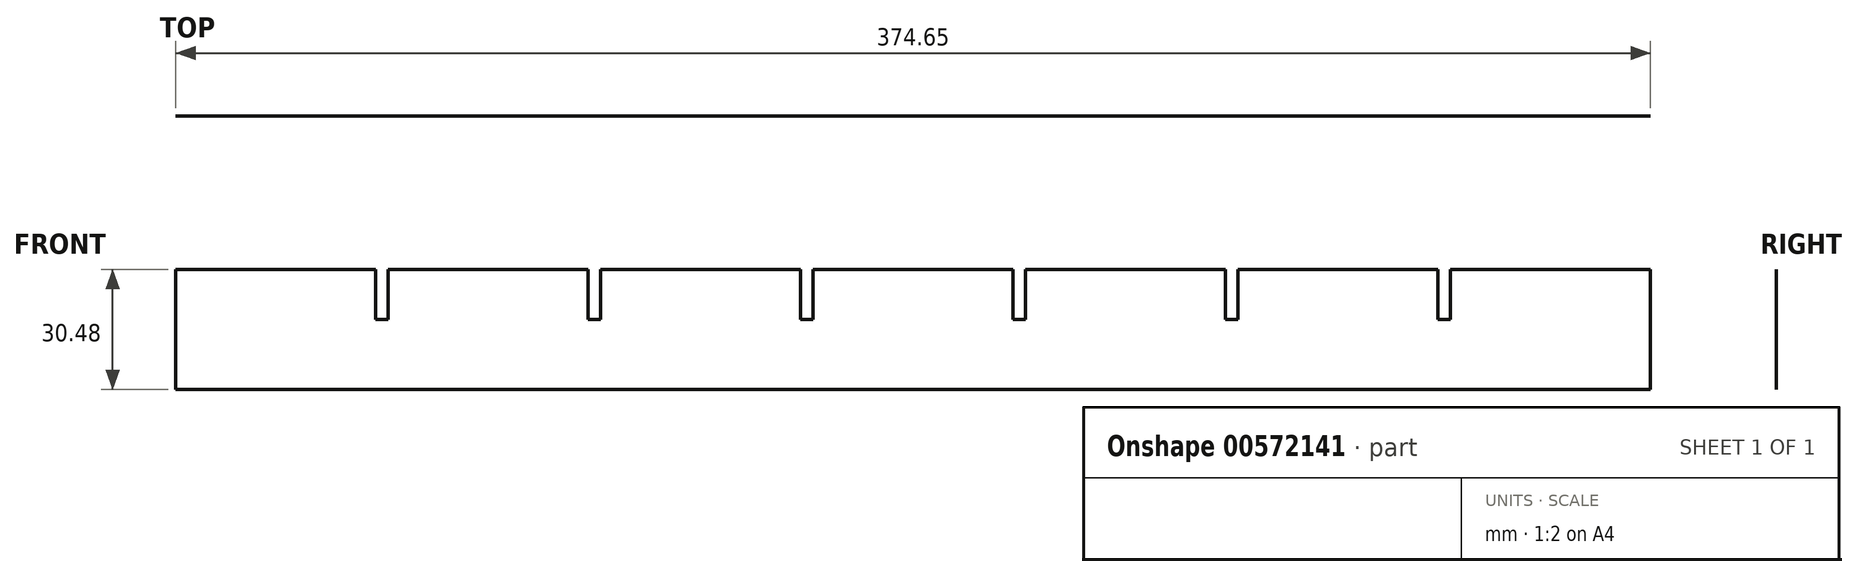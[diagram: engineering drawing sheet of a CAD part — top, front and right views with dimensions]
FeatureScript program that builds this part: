
annotation { "Feature Type Name" : "Feature", "Feature Type Description" : "" }
export const myFeature = defineFeature(function(context is Context, id is Id, definition is map)
    precondition{}
    {
        {
            var Q0;
            Q0=qCreatedBy(makeId("Front.planeOp"),FACE);
            var sketch = newSketch(context, id + "F0", { "sketchPlane" : qUnion([Q0])});
            skLineSegment(sketch, "E0.bottom", {"start": v(-281.33, -49.02) * mm, "end": v(93.32, -49.02) * mm});
            skLineSegment(sketch, "E0.top", {"start": v(-281.33, -79.5) * mm, "end": v(93.32, -79.5) * mm});
            skLineSegment(sketch, "E0.left", {"start": v(-281.33, -49.02) * mm, "end": v(-281.33, -79.5) * mm});
            skLineSegment(sketch, "E0.right", {"start": v(93.32, -49.02) * mm, "end": v(93.32, -79.5) * mm});
            skLineSegment(sketch, "E1", {"start": v(-230.53, -49.02) * mm, "end": v(-230.53, -61.72) * mm});
            skLineSegment(sketch, "E2", {"start": v(-230.53, -61.72) * mm, "end": v(-227.36, -61.72) * mm});
            skLineSegment(sketch, "E3", {"start": v(-227.36, -61.72) * mm, "end": v(-227.36, -49.02) * mm});
            skLineSegment(sketch, "E4", {"start": v(-176.56, -49.02) * mm, "end": v(-176.56, -61.72) * mm});
            skLineSegment(sketch, "E5", {"start": v(-176.56, -61.72) * mm, "end": v(-173.38, -61.72) * mm});
            skLineSegment(sketch, "E6", {"start": v(-173.38, -61.72) * mm, "end": v(-173.38, -49.02) * mm});
            skLineSegment(sketch, "E7", {"start": v(-122.58, -49.02) * mm, "end": v(-122.58, -61.72) * mm});
            skLineSegment(sketch, "E8", {"start": v(-122.58, -61.72) * mm, "end": v(-119.4, -61.72) * mm});
            skLineSegment(sketch, "E9", {"start": v(-119.4, -61.72) * mm, "end": v(-119.4, -49.02) * mm});
            skLineSegment(sketch, "E10", {"start": v(-68.6, -49.02) * mm, "end": v(-68.6, -61.72) * mm});
            skLineSegment(sketch, "E11", {"start": v(-68.6, -61.72) * mm, "end": v(-65.43, -61.72) * mm});
            skLineSegment(sketch, "E12", {"start": v(-65.43, -61.72) * mm, "end": v(-65.43, -49.02) * mm});
            skLineSegment(sketch, "E13", {"start": v(-14.63, -49.02) * mm, "end": v(-14.63, -61.72) * mm});
            skLineSegment(sketch, "E14", {"start": v(-14.63, -61.72) * mm, "end": v(-11.46, -61.72) * mm});
            skLineSegment(sketch, "E15", {"start": v(-11.46, -61.72) * mm, "end": v(-11.46, -49.02) * mm});
            skLineSegment(sketch, "E16", {"start": v(42.52, -49.02) * mm, "end": v(42.52, -61.72) * mm});
            skLineSegment(sketch, "E17", {"start": v(39.34, -61.72) * mm, "end": v(42.52, -61.72) * mm});
            skLineSegment(sketch, "E18", {"start": v(39.34, -61.72) * mm, "end": v(39.34, -49.02) * mm});
            skLineSegment(sketch, "E19", {"start": v(93.32, -49.02) * mm, "end": v(93.32, -61.72) * mm});
            skLineSegment(sketch, "E20", {"start": v(93.32, -61.72) * mm, "end": v(96.5, -61.72) * mm});
            skLineSegment(sketch, "E21", {"start": v(96.5, -61.72) * mm, "end": v(96.5, -49.02) * mm});
            skSolve(sketch);
        }
        {
            var Q0;
            Q0=makeQuery(id+"F0.imprint","IMPRINT",FACE,{"disambiguationData":[TD([[makeQuery(id+"F0.imprint","IMPRINT",EDGE,{"derivedFrom":sQuery(id+"F0.wireOp",EDGE,"E0.top")}),1.0]])]});
            extrude(context, id + "F1", {"entities" : qUnion([Q0]), "depth" : 1 / 203.2 * mm, "offsetDistance" : 25.4 * mm});
        }
    });
